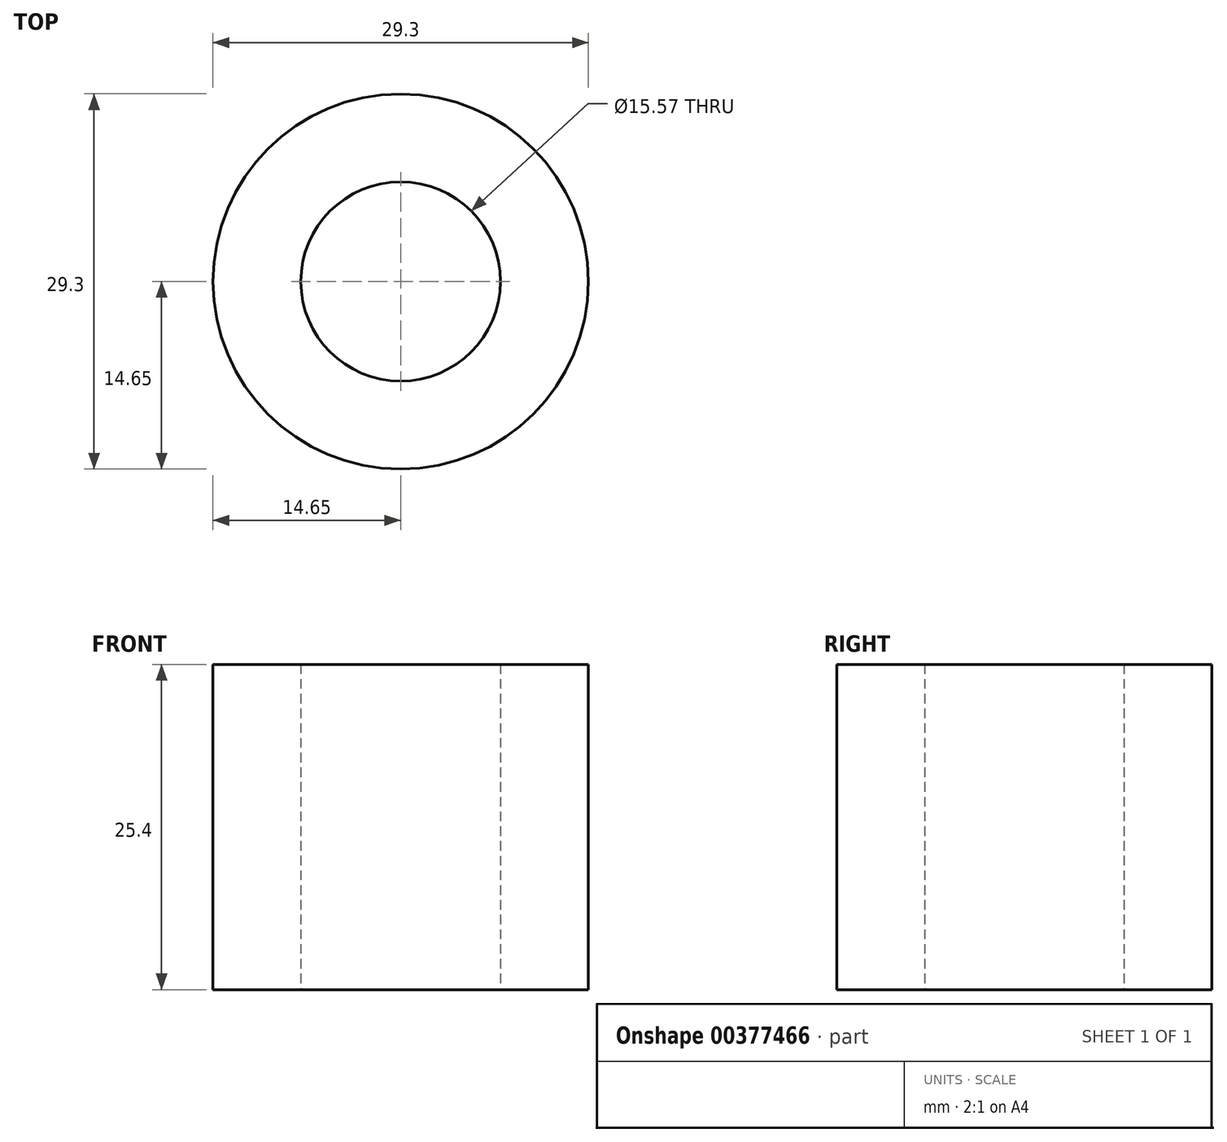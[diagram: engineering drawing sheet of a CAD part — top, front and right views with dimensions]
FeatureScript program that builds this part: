
annotation { "Feature Type Name" : "Feature", "Feature Type Description" : "" }
export const myFeature = defineFeature(function(context is Context, id is Id, definition is map)
    precondition{}
    {
        {
            var Q0;
            Q0=qCreatedBy(makeId("Top.planeOp"),FACE);
            var sketch = newSketch(context, id + "F0", { "sketchPlane" : qUnion([Q0])});
            skCircle(sketch, "E0", {"center": v(0, 0) * mm, "radius": 14.65 * mm});
            skCircle(sketch, "E1", {"center": v(0, 0) * mm, "radius": 7.78 * mm});
            skSolve(sketch);
        }
        {
            var Q0;
            Q0 = qSketchRegion(id + "F0", true);
            extrude(context, id + "F1", {"entities" : qUnion([Q0]), "depth" : 25.4 * mm});
        }
    });
